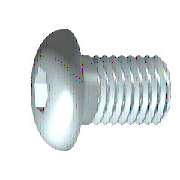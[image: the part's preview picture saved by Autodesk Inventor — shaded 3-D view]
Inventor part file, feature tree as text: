
AUTODESK INVENTOR PART (.ipt)
format: ipt  version: 2023.4 (Build 274418000, 418)  size: 200,192 bytes
history: native  units: mm (DEFAULTED — no unit token found)
features: extrude x1, plane x1, fillet x1
ambient origin geometry x7: Origin, YZ Plane, XY Plane, X Axis, Y Axis, Z Axis, Center Point
bodies: Solid1 (feature_tree), Body (feature_tree)
feature tree (3):
  extrude  "Slot"  Depth=4.2416mm
  plane  "Work Plane1"
  fillet  "Fillet2"  Radius=2.1083mm
